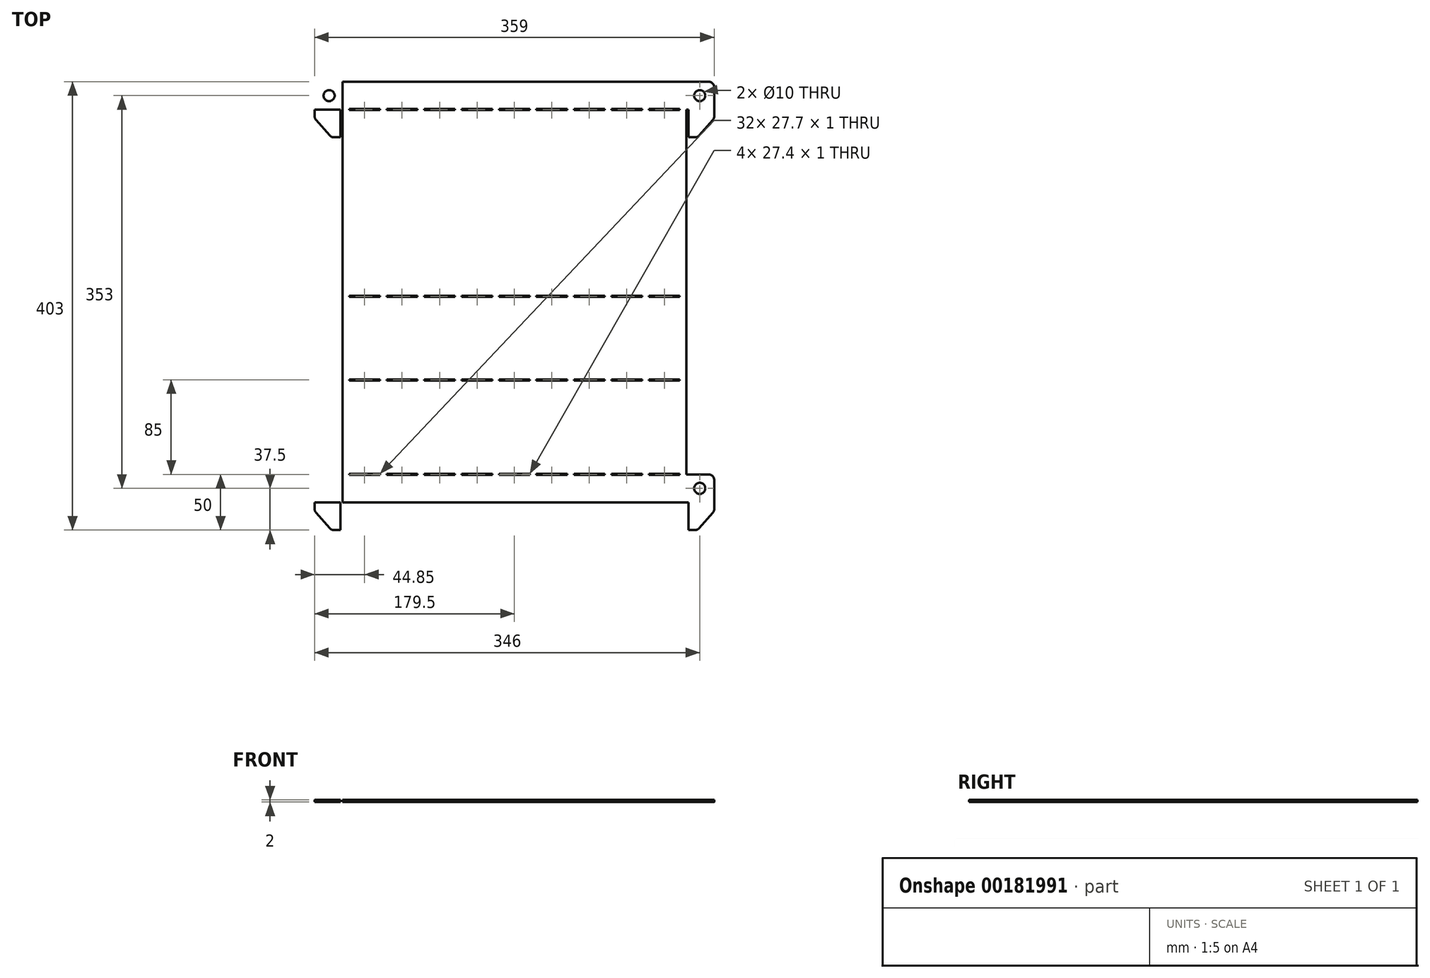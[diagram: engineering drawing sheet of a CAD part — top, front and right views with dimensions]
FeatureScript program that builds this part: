
annotation { "Feature Type Name" : "Feature", "Feature Type Description" : "" }
export const myFeature = defineFeature(function(context is Context, id is Id, definition is map)
    precondition{}
    {
        {
            var Q0;
            Q0=qCreatedBy(makeId("Top.planeOp"),FACE);
            var sketch = newSketch(context, id + "F0", { "sketchPlane" : qUnion([Q0])});
            skLineSegment(sketch, "E0.bottom", {"start": v(0, 0) * mm, "end": v(154.5, 0) * mm});
            skLineSegment(sketch, "E0.top", {"start": v(0, 378) * mm, "end": v(154.5, 378) * mm});
            skLineSegment(sketch, "E0.left", {"start": v(0, 0) * mm, "end": v(0, 352.5) * mm});
            skLineSegment(sketch, "E0.right", {"start": v(154.5, 0) * mm, "end": v(154.5, 378) * mm});
            skCircle(sketch, "E1", {"center": v(166.5, 365.5) * mm, "radius": 5 * mm});
            skLineSegment(sketch, "E2", {"start": v(154.5, 378) * mm, "end": v(174.5, 378) * mm});
            skLineSegment(sketch, "E3", {"start": v(154.5, 353) * mm, "end": v(0, 353) * mm});
            skLineSegment(sketch, "E4", {"start": v(0, 185) * mm, "end": v(148.5, 185) * mm});
            skLineSegment(sketch, "E5", {"start": v(0, 110) * mm, "end": v(154.5, 110) * mm});
            skLineSegment(sketch, "E6", {"start": v(0, 25) * mm, "end": v(154.5, 25) * mm});
            skPoint(sketch, "E7.visualSharp", {"position": v(179.5, 353) * mm});
            skLineSegment(sketch, "E8.bottom", {"start": v(148.5, 353) * mm, "end": v(120.8, 353) * mm});
            skLineSegment(sketch, "E8.top", {"start": v(148.5, 352.5) * mm, "end": v(120.8, 352.5) * mm});
            skLineSegment(sketch, "E8.left", {"start": v(148.5, 353) * mm, "end": v(148.5, 352.5) * mm});
            skLineSegment(sketch, "E8.right", {"start": v(120.8, 353) * mm, "end": v(120.8, 352.5) * mm});
            skLineSegment(sketch, "E9.bottom", {"start": v(114.8, 353) * mm, "end": v(87.1, 353) * mm});
            skLineSegment(sketch, "E9.top", {"start": v(114.8, 352.5) * mm, "end": v(87.1, 352.5) * mm});
            skLineSegment(sketch, "E9.left", {"start": v(114.8, 353) * mm, "end": v(114.8, 352.5) * mm});
            skLineSegment(sketch, "E9.right", {"start": v(87.1, 353) * mm, "end": v(87.1, 352.5) * mm});
            skLineSegment(sketch, "E10.bottom", {"start": v(81.1, 353) * mm, "end": v(53.4, 353) * mm});
            skLineSegment(sketch, "E10.top", {"start": v(81.1, 352.5) * mm, "end": v(53.4, 352.5) * mm});
            skLineSegment(sketch, "E10.left", {"start": v(81.1, 353) * mm, "end": v(81.1, 352.5) * mm});
            skLineSegment(sketch, "E10.right", {"start": v(53.4, 353) * mm, "end": v(53.4, 352.5) * mm});
            skLineSegment(sketch, "E11.bottom", {"start": v(47.4, 353) * mm, "end": v(19.7, 353) * mm});
            skLineSegment(sketch, "E11.top", {"start": v(47.4, 352.5) * mm, "end": v(19.7, 352.5) * mm});
            skLineSegment(sketch, "E11.left", {"start": v(47.4, 353) * mm, "end": v(47.4, 352.5) * mm});
            skLineSegment(sketch, "E11.right", {"start": v(19.7, 353) * mm, "end": v(19.7, 352.5) * mm});
            skLineSegment(sketch, "E12.bottom", {"start": v(13.7, 353) * mm, "end": v(0, 353) * mm});
            skLineSegment(sketch, "E12.top", {"start": v(13.7, 352.5) * mm, "end": v(0, 352.5) * mm});
            skLineSegment(sketch, "E12.left", {"start": v(13.7, 353) * mm, "end": v(13.7, 352.5) * mm});
            skLineSegment(sketch, "E12.right", {"start": v(0, 353) * mm, "end": v(0, 352.5) * mm});
            skLineSegment(sketch, "E13.MirrorCS", {"start": v(120.8, 353) * mm, "end": v(120.8, 353.5) * mm});
            skLineSegment(sketch, "E14.MirrorCS", {"start": v(148.5, 353.5) * mm, "end": v(120.8, 353.5) * mm});
            skLineSegment(sketch, "E15.MirrorCS", {"start": v(148.5, 353) * mm, "end": v(148.5, 353.5) * mm});
            skLineSegment(sketch, "E16.MirrorCS", {"start": v(114.8, 353) * mm, "end": v(114.8, 353.5) * mm});
            skLineSegment(sketch, "E17.MirrorCS", {"start": v(114.8, 353.5) * mm, "end": v(87.1, 353.5) * mm});
            skLineSegment(sketch, "E18.MirrorCS", {"start": v(87.1, 353) * mm, "end": v(87.1, 353.5) * mm});
            skLineSegment(sketch, "E19.MirrorCS", {"start": v(81.1, 353) * mm, "end": v(81.1, 353.5) * mm});
            skLineSegment(sketch, "E20.MirrorCS", {"start": v(81.1, 353.5) * mm, "end": v(53.4, 353.5) * mm});
            skLineSegment(sketch, "E21.MirrorCS", {"start": v(53.4, 353) * mm, "end": v(53.4, 353.5) * mm});
            skLineSegment(sketch, "E22.MirrorCS", {"start": v(47.4, 353) * mm, "end": v(47.4, 353.5) * mm});
            skLineSegment(sketch, "E23.MirrorCS", {"start": v(47.4, 353.5) * mm, "end": v(19.7, 353.5) * mm});
            skLineSegment(sketch, "E24.MirrorCS", {"start": v(19.7, 353) * mm, "end": v(19.7, 353.5) * mm});
            skLineSegment(sketch, "E25.MirrorCS", {"start": v(13.7, 353) * mm, "end": v(13.7, 353.5) * mm});
            skLineSegment(sketch, "E26.MirrorCS", {"start": v(13.7, 353.5) * mm, "end": v(0, 353.5) * mm});
            skLineSegment(sketch, "E27.MirrorCS", {"start": v(0, 353) * mm, "end": v(0, 353.5) * mm});
            skLineSegment(sketch, "E28", {"start": v(111.78, 185) * mm, "end": v(0, 185) * mm});
            skLineSegment(sketch, "E29.bottom", {"start": v(148.5, 185) * mm, "end": v(120.8, 185) * mm});
            skLineSegment(sketch, "E29.top", {"start": v(148.5, 184.5) * mm, "end": v(120.8, 184.5) * mm});
            skLineSegment(sketch, "E29.left", {"start": v(148.5, 185) * mm, "end": v(148.5, 184.5) * mm});
            skLineSegment(sketch, "E29.right", {"start": v(120.8, 185) * mm, "end": v(120.8, 184.5) * mm});
            skLineSegment(sketch, "E30.bottom", {"start": v(114.8, 185) * mm, "end": v(87.1, 185) * mm});
            skLineSegment(sketch, "E30.top", {"start": v(114.8, 184.5) * mm, "end": v(87.1, 184.5) * mm});
            skLineSegment(sketch, "E30.left", {"start": v(114.8, 185) * mm, "end": v(114.8, 184.5) * mm});
            skLineSegment(sketch, "E30.right", {"start": v(87.1, 185) * mm, "end": v(87.1, 184.5) * mm});
            skLineSegment(sketch, "E31.bottom", {"start": v(81.1, 185) * mm, "end": v(53.4, 185) * mm});
            skLineSegment(sketch, "E31.top", {"start": v(81.1, 184.5) * mm, "end": v(53.4, 184.5) * mm});
            skLineSegment(sketch, "E31.left", {"start": v(81.1, 185) * mm, "end": v(81.1, 184.5) * mm});
            skLineSegment(sketch, "E31.right", {"start": v(53.4, 185) * mm, "end": v(53.4, 184.5) * mm});
            skLineSegment(sketch, "E32.bottom", {"start": v(47.4, 185) * mm, "end": v(19.7, 185) * mm});
            skLineSegment(sketch, "E32.top", {"start": v(47.4, 184.5) * mm, "end": v(19.7, 184.5) * mm});
            skLineSegment(sketch, "E32.left", {"start": v(47.4, 185) * mm, "end": v(47.4, 184.5) * mm});
            skLineSegment(sketch, "E32.right", {"start": v(19.7, 185) * mm, "end": v(19.7, 184.5) * mm});
            skLineSegment(sketch, "E33.bottom", {"start": v(13.7, 185) * mm, "end": v(0, 185) * mm});
            skLineSegment(sketch, "E33.top", {"start": v(13.7, 184.5) * mm, "end": v(0, 184.5) * mm});
            skLineSegment(sketch, "E33.left", {"start": v(13.7, 185) * mm, "end": v(13.7, 184.5) * mm});
            skLineSegment(sketch, "E34.MirrorCS", {"start": v(120.8, 185) * mm, "end": v(120.8, 185.5) * mm});
            skLineSegment(sketch, "E35.MirrorCS", {"start": v(148.5, 185.5) * mm, "end": v(120.8, 185.5) * mm});
            skLineSegment(sketch, "E36.MirrorCS", {"start": v(148.5, 185) * mm, "end": v(148.5, 185.5) * mm});
            skLineSegment(sketch, "E37.MirrorCS", {"start": v(114.8, 185) * mm, "end": v(114.8, 185.5) * mm});
            skLineSegment(sketch, "E38.MirrorCS", {"start": v(114.8, 185.5) * mm, "end": v(87.1, 185.5) * mm});
            skLineSegment(sketch, "E39.MirrorCS", {"start": v(87.1, 185) * mm, "end": v(87.1, 185.5) * mm});
            skLineSegment(sketch, "E40.MirrorCS", {"start": v(81.1, 185) * mm, "end": v(81.1, 185.5) * mm});
            skLineSegment(sketch, "E41.MirrorCS", {"start": v(81.1, 185.5) * mm, "end": v(53.4, 185.5) * mm});
            skLineSegment(sketch, "E42.MirrorCS", {"start": v(53.4, 185) * mm, "end": v(53.4, 185.5) * mm});
            skLineSegment(sketch, "E43.MirrorCS", {"start": v(47.4, 185) * mm, "end": v(47.4, 185.5) * mm});
            skLineSegment(sketch, "E44.MirrorCS", {"start": v(47.4, 185.5) * mm, "end": v(19.7, 185.5) * mm});
            skLineSegment(sketch, "E45.MirrorCS", {"start": v(19.7, 185) * mm, "end": v(19.7, 185.5) * mm});
            skLineSegment(sketch, "E46.MirrorCS", {"start": v(13.7, 185) * mm, "end": v(13.7, 185.5) * mm});
            skLineSegment(sketch, "E47.MirrorCS", {"start": v(13.7, 185.5) * mm, "end": v(0, 185.5) * mm});
            skLineSegment(sketch, "E48", {"start": v(148.5, 110) * mm, "end": v(0, 110) * mm});
            skLineSegment(sketch, "E49.bottom", {"start": v(148.5, 110) * mm, "end": v(120.8, 110) * mm});
            skLineSegment(sketch, "E49.top", {"start": v(148.5, 109.5) * mm, "end": v(120.8, 109.5) * mm});
            skLineSegment(sketch, "E49.left", {"start": v(148.5, 110) * mm, "end": v(148.5, 109.5) * mm});
            skLineSegment(sketch, "E49.right", {"start": v(120.8, 110) * mm, "end": v(120.8, 109.5) * mm});
            skLineSegment(sketch, "E50.bottom", {"start": v(114.8, 110) * mm, "end": v(87.1, 110) * mm});
            skLineSegment(sketch, "E50.top", {"start": v(114.8, 109.5) * mm, "end": v(87.1, 109.5) * mm});
            skLineSegment(sketch, "E50.left", {"start": v(114.8, 110) * mm, "end": v(114.8, 109.5) * mm});
            skLineSegment(sketch, "E50.right", {"start": v(87.1, 110) * mm, "end": v(87.1, 109.5) * mm});
            skLineSegment(sketch, "E51.bottom", {"start": v(81.1, 110) * mm, "end": v(53.4, 110) * mm});
            skLineSegment(sketch, "E51.top", {"start": v(81.1, 109.5) * mm, "end": v(53.4, 109.5) * mm});
            skLineSegment(sketch, "E51.left", {"start": v(81.1, 110) * mm, "end": v(81.1, 109.5) * mm});
            skLineSegment(sketch, "E51.right", {"start": v(53.4, 110) * mm, "end": v(53.4, 109.5) * mm});
            skLineSegment(sketch, "E52.bottom", {"start": v(47.4, 110) * mm, "end": v(19.7, 110) * mm});
            skLineSegment(sketch, "E52.top", {"start": v(47.4, 109.5) * mm, "end": v(19.7, 109.5) * mm});
            skLineSegment(sketch, "E52.left", {"start": v(47.4, 110) * mm, "end": v(47.4, 109.5) * mm});
            skLineSegment(sketch, "E52.right", {"start": v(19.7, 110) * mm, "end": v(19.7, 109.5) * mm});
            skLineSegment(sketch, "E53.bottom", {"start": v(13.7, 110) * mm, "end": v(0, 110) * mm});
            skLineSegment(sketch, "E53.top", {"start": v(13.7, 109.5) * mm, "end": v(0, 109.5) * mm});
            skLineSegment(sketch, "E53.left", {"start": v(13.7, 110) * mm, "end": v(13.7, 109.5) * mm});
            skLineSegment(sketch, "E54.MirrorCS", {"start": v(120.8, 110) * mm, "end": v(120.8, 110.5) * mm});
            skLineSegment(sketch, "E55.MirrorCS", {"start": v(148.5, 110.5) * mm, "end": v(120.8, 110.5) * mm});
            skLineSegment(sketch, "E56.MirrorCS", {"start": v(148.5, 110) * mm, "end": v(148.5, 110.5) * mm});
            skLineSegment(sketch, "E57.MirrorCS", {"start": v(114.8, 110) * mm, "end": v(114.8, 110.5) * mm});
            skLineSegment(sketch, "E58.MirrorCS", {"start": v(114.8, 110.5) * mm, "end": v(87.1, 110.5) * mm});
            skLineSegment(sketch, "E59.MirrorCS", {"start": v(87.1, 110) * mm, "end": v(87.1, 110.5) * mm});
            skLineSegment(sketch, "E60.MirrorCS", {"start": v(81.1, 110) * mm, "end": v(81.1, 110.5) * mm});
            skLineSegment(sketch, "E61.MirrorCS", {"start": v(81.1, 110.5) * mm, "end": v(53.4, 110.5) * mm});
            skLineSegment(sketch, "E62.MirrorCS", {"start": v(53.4, 110) * mm, "end": v(53.4, 110.5) * mm});
            skLineSegment(sketch, "E63.MirrorCS", {"start": v(47.4, 110) * mm, "end": v(47.4, 110.5) * mm});
            skLineSegment(sketch, "E64.MirrorCS", {"start": v(47.4, 110.5) * mm, "end": v(19.7, 110.5) * mm});
            skLineSegment(sketch, "E65.MirrorCS", {"start": v(19.7, 110) * mm, "end": v(19.7, 110.5) * mm});
            skLineSegment(sketch, "E66.MirrorCS", {"start": v(13.7, 110) * mm, "end": v(13.7, 110.5) * mm});
            skLineSegment(sketch, "E67.MirrorCS", {"start": v(13.7, 110.5) * mm, "end": v(0, 110.5) * mm});
            skLineSegment(sketch, "E68", {"start": v(148.5, 25) * mm, "end": v(0, 25) * mm});
            skLineSegment(sketch, "E69.bottom", {"start": v(148.5, 25) * mm, "end": v(120.8, 25) * mm});
            skLineSegment(sketch, "E69.top", {"start": v(148.5, 24.5) * mm, "end": v(120.8, 24.5) * mm});
            skLineSegment(sketch, "E69.left", {"start": v(148.5, 25) * mm, "end": v(148.5, 24.5) * mm});
            skLineSegment(sketch, "E69.right", {"start": v(120.8, 25) * mm, "end": v(120.8, 24.5) * mm});
            skLineSegment(sketch, "E70.bottom", {"start": v(114.8, 25) * mm, "end": v(87.1, 25) * mm});
            skLineSegment(sketch, "E70.top", {"start": v(114.8, 24.5) * mm, "end": v(87.1, 24.5) * mm});
            skLineSegment(sketch, "E70.left", {"start": v(114.8, 25) * mm, "end": v(114.8, 24.5) * mm});
            skLineSegment(sketch, "E70.right", {"start": v(87.1, 25) * mm, "end": v(87.1, 24.5) * mm});
            skLineSegment(sketch, "E71.bottom", {"start": v(81.1, 25) * mm, "end": v(53.4, 25) * mm});
            skLineSegment(sketch, "E71.top", {"start": v(81.1, 24.5) * mm, "end": v(53.4, 24.5) * mm});
            skLineSegment(sketch, "E71.left", {"start": v(81.1, 25) * mm, "end": v(81.1, 24.5) * mm});
            skLineSegment(sketch, "E71.right", {"start": v(53.4, 25) * mm, "end": v(53.4, 24.5) * mm});
            skLineSegment(sketch, "E72.bottom", {"start": v(47.4, 25) * mm, "end": v(19.7, 25) * mm});
            skLineSegment(sketch, "E72.top", {"start": v(47.4, 24.5) * mm, "end": v(19.7, 24.5) * mm});
            skLineSegment(sketch, "E72.left", {"start": v(47.4, 25) * mm, "end": v(47.4, 24.5) * mm});
            skLineSegment(sketch, "E72.right", {"start": v(19.7, 25) * mm, "end": v(19.7, 24.5) * mm});
            skLineSegment(sketch, "E73.bottom", {"start": v(13.7, 25) * mm, "end": v(0, 25) * mm});
            skLineSegment(sketch, "E73.top", {"start": v(13.7, 24.5) * mm, "end": v(0, 24.5) * mm});
            skLineSegment(sketch, "E73.left", {"start": v(13.7, 25) * mm, "end": v(13.7, 24.5) * mm});
            skLineSegment(sketch, "E74.MirrorCS", {"start": v(120.8, 25) * mm, "end": v(120.8, 25.5) * mm});
            skLineSegment(sketch, "E75.MirrorCS", {"start": v(148.5, 25.5) * mm, "end": v(120.8, 25.5) * mm});
            skLineSegment(sketch, "E76.MirrorCS", {"start": v(148.5, 25) * mm, "end": v(148.5, 25.5) * mm});
            skLineSegment(sketch, "E77.MirrorCS", {"start": v(114.8, 25) * mm, "end": v(114.8, 25.5) * mm});
            skLineSegment(sketch, "E78.MirrorCS", {"start": v(114.8, 25.5) * mm, "end": v(87.1, 25.5) * mm});
            skLineSegment(sketch, "E79.MirrorCS", {"start": v(87.1, 25) * mm, "end": v(87.1, 25.5) * mm});
            skLineSegment(sketch, "E80.MirrorCS", {"start": v(81.1, 25) * mm, "end": v(81.1, 25.5) * mm});
            skLineSegment(sketch, "E81.MirrorCS", {"start": v(81.1, 25.5) * mm, "end": v(53.4, 25.5) * mm});
            skLineSegment(sketch, "E82.MirrorCS", {"start": v(53.4, 25) * mm, "end": v(53.4, 25.5) * mm});
            skLineSegment(sketch, "E83.MirrorCS", {"start": v(47.4, 25) * mm, "end": v(47.4, 25.5) * mm});
            skLineSegment(sketch, "E84.MirrorCS", {"start": v(47.4, 25.5) * mm, "end": v(19.7, 25.5) * mm});
            skLineSegment(sketch, "E85.MirrorCS", {"start": v(19.7, 25) * mm, "end": v(19.7, 25.5) * mm});
            skLineSegment(sketch, "E86.MirrorCS", {"start": v(13.7, 25) * mm, "end": v(13.7, 25.5) * mm});
            skLineSegment(sketch, "E87.MirrorCS", {"start": v(13.7, 25.5) * mm, "end": v(0, 25.5) * mm});
            skLineSegment(sketch, "E88", {"start": v(154.5, 25) * mm, "end": v(174.5, 25) * mm});
            skLineSegment(sketch, "E89", {"start": v(179.5, 20) * mm, "end": v(179.5, 0) * mm});
            skLineSegment(sketch, "E90", {"start": v(179.5, 0) * mm, "end": v(154.5, 0) * mm});
            skLineSegment(sketch, "E91", {"start": v(156.5, 0) * mm, "end": v(156.5, -25) * mm});
            skLineSegment(sketch, "E92", {"start": v(156.5, -25) * mm, "end": v(162.24, -25) * mm});
            skLineSegment(sketch, "E93", {"start": v(179.5, 0) * mm, "end": v(179.5, -6.1) * mm});
            skLineSegment(sketch, "E94", {"start": v(178.25, -9.42) * mm, "end": v(166, -23.3) * mm});
            skCircle(sketch, "E95", {"center": v(166.5, 12.5) * mm, "radius": 5 * mm});
            skPoint(sketch, "E96.visualSharp", {"position": v(179.5, 25) * mm});
            skArc(sketch, "E96.filletArc", {"start": v(179.5, 20) * mm, "mid": v(178.04, 23.54) * mm, "end": v(174.5, 25) * mm});
            skPoint(sketch, "E97.visualSharp", {"position": v(179.5, -8) * mm});
            skArc(sketch, "E97.filletArc", {"start": v(178.25, -9.42) * mm, "mid": v(179.18, -7.88) * mm, "end": v(179.5, -6.1) * mm});
            skPoint(sketch, "E98.visualSharp", {"position": v(164.5, -25) * mm});
            skArc(sketch, "E98.filletArc", {"start": v(162.24, -25) * mm, "mid": v(164.3, -24.56) * mm, "end": v(166, -23.3) * mm});
            skLineSegment(sketch, "E99.MirrorCS", {"start": v(-148.5, 25) * mm, "end": v(-148.5, 24.5) * mm});
            skLineSegment(sketch, "E100.MirrorCS", {"start": v(-13.7, 353.5) * mm, "end": v(0, 353.5) * mm});
            skLineSegment(sketch, "E101.MirrorCS", {"start": v(-13.7, 353) * mm, "end": v(-13.7, 352.5) * mm});
            skLineSegment(sketch, "E102.MirrorCS", {"start": v(-148.5, 185) * mm, "end": v(-148.5, 184.5) * mm});
            skLineSegment(sketch, "E103.MirrorCS", {"start": v(-114.8, 185) * mm, "end": v(-114.8, 184.5) * mm});
            skLineSegment(sketch, "E104.MirrorCS", {"start": v(-81.1, 353) * mm, "end": v(-81.1, 353.5) * mm});
            skLineSegment(sketch, "E105.MirrorCS", {"start": v(-13.7, 352.5) * mm, "end": v(0, 352.5) * mm});
            skLineSegment(sketch, "E106.MirrorCS", {"start": v(-81.1, 25) * mm, "end": v(-81.1, 25.5) * mm});
            skLineSegment(sketch, "E107.MirrorCS", {"start": v(-53.4, 110) * mm, "end": v(-53.4, 110.5) * mm});
            skLineSegment(sketch, "E108.MirrorCS", {"start": v(-114.8, 110) * mm, "end": v(-114.8, 110.5) * mm});
            skLineSegment(sketch, "E109.MirrorCS", {"start": v(-148.5, 353) * mm, "end": v(-148.5, 352.5) * mm});
            skLineSegment(sketch, "E110.MirrorCS", {"start": v(-47.4, 185) * mm, "end": v(-47.4, 184.5) * mm});
            skLineSegment(sketch, "E111.MirrorCS", {"start": v(-47.4, 110) * mm, "end": v(-47.4, 110.5) * mm});
            skLineSegment(sketch, "E112.MirrorCS", {"start": v(-47.4, 353) * mm, "end": v(-47.4, 353.5) * mm});
            skLineSegment(sketch, "E113.MirrorCS", {"start": v(-148.5, 25) * mm, "end": v(-148.5, 25.5) * mm});
            skLineSegment(sketch, "E114.MirrorCS", {"start": v(-120.8, 353) * mm, "end": v(-120.8, 352.5) * mm});
            skLineSegment(sketch, "E115.MirrorCS", {"start": v(-53.4, 25) * mm, "end": v(-53.4, 25.5) * mm});
            skLineSegment(sketch, "E116.MirrorCS", {"start": v(-47.4, 25) * mm, "end": v(-47.4, 25.5) * mm});
            skLineSegment(sketch, "E117.MirrorCS", {"start": v(-19.7, 110) * mm, "end": v(-19.7, 110.5) * mm});
            skLineSegment(sketch, "E118.MirrorCS", {"start": v(-13.7, 110) * mm, "end": v(-13.7, 110.5) * mm});
            skLineSegment(sketch, "E119.MirrorCS", {"start": v(-114.8, 353) * mm, "end": v(-114.8, 352.5) * mm});
            skLineSegment(sketch, "E120.MirrorCS", {"start": v(-114.8, 25) * mm, "end": v(-114.8, 25.5) * mm});
            skLineSegment(sketch, "E121.MirrorCS", {"start": v(-19.7, 25) * mm, "end": v(-19.7, 25.5) * mm});
            skLineSegment(sketch, "E122.MirrorCS", {"start": v(-120.8, 185) * mm, "end": v(-120.8, 184.5) * mm});
            skLineSegment(sketch, "E123.MirrorCS", {"start": v(-87.1, 353) * mm, "end": v(-87.1, 352.5) * mm});
            skLineSegment(sketch, "E124.MirrorCS", {"start": v(-13.7, 25) * mm, "end": v(-13.7, 25.5) * mm});
            skLineSegment(sketch, "E125.MirrorCS", {"start": v(-148.5, 110) * mm, "end": v(-148.5, 109.5) * mm});
            skLineSegment(sketch, "E126.MirrorCS", {"start": v(-120.8, 110) * mm, "end": v(-120.8, 110.5) * mm});
            skLineSegment(sketch, "E127.MirrorCS", {"start": v(-148.5, 185) * mm, "end": v(-148.5, 185.5) * mm});
            skLineSegment(sketch, "E128.MirrorCS", {"start": v(-19.7, 353) * mm, "end": v(-19.7, 353.5) * mm});
            skLineSegment(sketch, "E129.MirrorCS", {"start": v(-87.1, 185) * mm, "end": v(-87.1, 184.5) * mm});
            skLineSegment(sketch, "E130.MirrorCS", {"start": v(-87.1, 25) * mm, "end": v(-87.1, 24.5) * mm});
            skLineSegment(sketch, "E131.MirrorCS", {"start": v(-81.1, 110) * mm, "end": v(-81.1, 110.5) * mm});
            skLineSegment(sketch, "E132.MirrorCS", {"start": v(-53.4, 353) * mm, "end": v(-53.4, 352.5) * mm});
            skLineSegment(sketch, "E133.MirrorCS", {"start": v(-120.8, 25) * mm, "end": v(-120.8, 25.5) * mm});
            skLineSegment(sketch, "E134.MirrorCS", {"start": v(-148.5, 110) * mm, "end": v(-148.5, 110.5) * mm});
            skLineSegment(sketch, "E135.MirrorCS", {"start": v(-13.7, 353) * mm, "end": v(-13.7, 353.5) * mm});
            skLineSegment(sketch, "E136.MirrorCS", {"start": v(-81.1, 353) * mm, "end": v(-81.1, 352.5) * mm});
            skLineSegment(sketch, "E137.MirrorCS", {"start": v(-114.8, 185) * mm, "end": v(-114.8, 185.5) * mm});
            skLineSegment(sketch, "E138.MirrorCS", {"start": v(-13.7, 25) * mm, "end": v(-13.7, 24.5) * mm});
            skLineSegment(sketch, "E139.MirrorCS", {"start": v(-87.1, 185) * mm, "end": v(-87.1, 185.5) * mm});
            skLineSegment(sketch, "E140.MirrorCS", {"start": v(-53.4, 353) * mm, "end": v(-53.4, 353.5) * mm});
            skLineSegment(sketch, "E141.MirrorCS", {"start": v(-53.4, 110) * mm, "end": v(-53.4, 109.5) * mm});
            skLineSegment(sketch, "E142.MirrorCS", {"start": v(-114.8, 110) * mm, "end": v(-114.8, 109.5) * mm});
            skLineSegment(sketch, "E143.MirrorCS", {"start": v(-19.7, 185) * mm, "end": v(-19.7, 185.5) * mm});
            skLineSegment(sketch, "E144.MirrorCS", {"start": v(-81.1, 25) * mm, "end": v(-81.1, 24.5) * mm});
            skLineSegment(sketch, "E145.MirrorCS", {"start": v(-81.1, 185) * mm, "end": v(-81.1, 185.5) * mm});
            skLineSegment(sketch, "E146.MirrorCS", {"start": v(-87.1, 110) * mm, "end": v(-87.1, 109.5) * mm});
            skLineSegment(sketch, "E147.MirrorCS", {"start": v(-13.7, 185) * mm, "end": v(-13.7, 185.5) * mm});
            skLineSegment(sketch, "E148.MirrorCS", {"start": v(-19.7, 185) * mm, "end": v(-19.7, 184.5) * mm});
            skLineSegment(sketch, "E149.MirrorCS", {"start": v(-53.4, 25) * mm, "end": v(-53.4, 24.5) * mm});
            skLineSegment(sketch, "E150.MirrorCS", {"start": v(-120.8, 353) * mm, "end": v(-120.8, 353.5) * mm});
            skLineSegment(sketch, "E151.MirrorCS", {"start": v(-47.4, 110) * mm, "end": v(-47.4, 109.5) * mm});
            skLineSegment(sketch, "E152.MirrorCS", {"start": v(-19.7, 110) * mm, "end": v(-19.7, 109.5) * mm});
            skLineSegment(sketch, "E153.MirrorCS", {"start": v(-148.5, 353) * mm, "end": v(-148.5, 353.5) * mm});
            skLineSegment(sketch, "E154.MirrorCS", {"start": v(-114.8, 25) * mm, "end": v(-114.8, 24.5) * mm});
            skLineSegment(sketch, "E155.MirrorCS", {"start": v(-87.1, 110) * mm, "end": v(-87.1, 110.5) * mm});
            skLineSegment(sketch, "E156.MirrorCS", {"start": v(-13.7, 185) * mm, "end": v(-13.7, 184.5) * mm});
            skLineSegment(sketch, "E157.MirrorCS", {"start": v(-47.4, 25) * mm, "end": v(-47.4, 24.5) * mm});
            skLineSegment(sketch, "E158.MirrorCS", {"start": v(-114.8, 353) * mm, "end": v(-114.8, 353.5) * mm});
            skLineSegment(sketch, "E159.MirrorCS", {"start": v(-120.8, 185) * mm, "end": v(-120.8, 185.5) * mm});
            skLineSegment(sketch, "E160.MirrorCS", {"start": v(-19.7, 25) * mm, "end": v(-19.7, 24.5) * mm});
            skLineSegment(sketch, "E161.MirrorCS", {"start": v(-13.7, 110) * mm, "end": v(-13.7, 109.5) * mm});
            skLineSegment(sketch, "E162.MirrorCS", {"start": v(-81.1, 185) * mm, "end": v(-81.1, 184.5) * mm});
            skLineSegment(sketch, "E163.MirrorCS", {"start": v(-47.4, 353) * mm, "end": v(-47.4, 352.5) * mm});
            skLineSegment(sketch, "E164.MirrorCS", {"start": v(-13.7, 25.5) * mm, "end": v(0, 25.5) * mm});
            skLineSegment(sketch, "E165.MirrorCS", {"start": v(-87.1, 353) * mm, "end": v(-87.1, 353.5) * mm});
            skLineSegment(sketch, "E166.MirrorCS", {"start": v(-120.8, 110) * mm, "end": v(-120.8, 109.5) * mm});
            skLineSegment(sketch, "E167.MirrorCS", {"start": v(-53.4, 185) * mm, "end": v(-53.4, 185.5) * mm});
            skLineSegment(sketch, "E168.MirrorCS", {"start": v(-53.4, 185) * mm, "end": v(-53.4, 184.5) * mm});
            skLineSegment(sketch, "E169.MirrorCS", {"start": v(-19.7, 353) * mm, "end": v(-19.7, 352.5) * mm});
            skLineSegment(sketch, "E170.MirrorCS", {"start": v(-120.8, 25) * mm, "end": v(-120.8, 24.5) * mm});
            skLineSegment(sketch, "E171.MirrorCS", {"start": v(-47.4, 185) * mm, "end": v(-47.4, 185.5) * mm});
            skLineSegment(sketch, "E172.MirrorCS", {"start": v(-13.7, 353) * mm, "end": v(0, 353) * mm});
            skLineSegment(sketch, "E173.MirrorCS", {"start": v(-87.1, 25) * mm, "end": v(-87.1, 25.5) * mm});
            skLineSegment(sketch, "E174.MirrorCS", {"start": v(-81.1, 110) * mm, "end": v(-81.1, 109.5) * mm});
            skLineSegment(sketch, "E175.MirrorCS", {"start": v(-13.7, 185) * mm, "end": v(0, 185) * mm});
            skLineSegment(sketch, "E176.MirrorCS", {"start": v(-13.7, 110.5) * mm, "end": v(0, 110.5) * mm});
            skLineSegment(sketch, "E177.MirrorCS", {"start": v(-13.7, 25) * mm, "end": v(0, 25) * mm});
            skLineSegment(sketch, "E178.MirrorCS", {"start": v(-13.7, 185.5) * mm, "end": v(0, 185.5) * mm});
            skLineSegment(sketch, "E179.MirrorCS", {"start": v(-13.7, 184.5) * mm, "end": v(0, 184.5) * mm});
            skLineSegment(sketch, "E180.MirrorCS", {"start": v(-13.7, 110) * mm, "end": v(0, 110) * mm});
            skLineSegment(sketch, "E181.MirrorCS", {"start": v(-13.7, 109.5) * mm, "end": v(0, 109.5) * mm});
            skLineSegment(sketch, "E182.MirrorCS", {"start": v(-13.7, 24.5) * mm, "end": v(0, 24.5) * mm});
            skLineSegment(sketch, "E183.MirrorCS", {"start": v(-47.4, 110) * mm, "end": v(-19.7, 110) * mm});
            skLineSegment(sketch, "E184.MirrorCS", {"start": v(-156.5, -25) * mm, "end": v(-162.24, -25) * mm});
            skArc(sketch, "E185.MirrorCS", {"start": v(-162.24, -25) * mm, "mid": v(-164.3, -24.56) * mm, "end": v(-166, -23.3) * mm});
            skLineSegment(sketch, "E186.MirrorCS", {"start": v(-47.4, 25) * mm, "end": v(-19.7, 25) * mm});
            skLineSegment(sketch, "E187.MirrorCS", {"start": v(-47.4, 185.5) * mm, "end": v(-19.7, 185.5) * mm});
            skLineSegment(sketch, "E188.MirrorCS", {"start": v(-81.1, 24.5) * mm, "end": v(-53.4, 24.5) * mm});
            skArc(sketch, "E189.MirrorCS", {"start": v(-178.25, -9.42) * mm, "mid": v(-179.18, -7.88) * mm, "end": v(-179.5, -6.1) * mm});
            skLineSegment(sketch, "E190.MirrorCS", {"start": v(-47.4, 110.5) * mm, "end": v(-19.7, 110.5) * mm});
            skLineSegment(sketch, "E191.MirrorCS", {"start": v(-114.8, 353) * mm, "end": v(-87.1, 353) * mm});
            skLineSegment(sketch, "E192.MirrorCS", {"start": v(-148.5, 185) * mm, "end": v(-120.8, 185) * mm});
            skLineSegment(sketch, "E193.MirrorCS", {"start": v(-47.4, 25.5) * mm, "end": v(-19.7, 25.5) * mm});
            skLineSegment(sketch, "E194.MirrorCS", {"start": v(-148.5, 110) * mm, "end": v(-120.8, 110) * mm});
            skLineSegment(sketch, "E195.MirrorCS", {"start": v(-179.5, 0) * mm, "end": v(-179.5, -6.1) * mm});
            skLineSegment(sketch, "E196.MirrorCS", {"start": v(-114.8, 185) * mm, "end": v(-87.1, 185) * mm});
            skLineSegment(sketch, "E197.MirrorCS", {"start": v(-81.1, 353) * mm, "end": v(-53.4, 353) * mm});
            skLineSegment(sketch, "E198.MirrorCS", {"start": v(-148.5, 25) * mm, "end": v(-120.8, 25) * mm});
            skLineSegment(sketch, "E199.MirrorCS", {"start": v(-178.25, -9.42) * mm, "end": v(-166, -23.3) * mm});
            skLineSegment(sketch, "E200.MirrorCS", {"start": v(-114.8, 109.5) * mm, "end": v(-87.1, 109.5) * mm});
            skLineSegment(sketch, "E201.MirrorCS", {"start": v(-114.8, 110) * mm, "end": v(-87.1, 110) * mm});
            skLineSegment(sketch, "E202.MirrorCS", {"start": v(-148.5, 352.5) * mm, "end": v(-120.8, 352.5) * mm});
            skLineSegment(sketch, "E203.MirrorCS", {"start": v(-81.1, 185) * mm, "end": v(-53.4, 185) * mm});
            skLineSegment(sketch, "E204.MirrorCS", {"start": v(-47.4, 353) * mm, "end": v(-19.7, 353) * mm});
            skLineSegment(sketch, "E205.MirrorCS", {"start": v(-47.4, 184.5) * mm, "end": v(-19.7, 184.5) * mm});
            skArc(sketch, "E206.MirrorCS", {"start": v(-179.5, 20) * mm, "mid": v(-178.04, 23.54) * mm, "end": v(-174.5, 25) * mm});
            skLineSegment(sketch, "E207.MirrorCS", {"start": v(-114.8, 25) * mm, "end": v(-87.1, 25) * mm});
            skLineSegment(sketch, "E208.MirrorCS", {"start": v(-81.1, 25.5) * mm, "end": v(-53.4, 25.5) * mm});
            skLineSegment(sketch, "E209.MirrorCS", {"start": v(-47.4, 109.5) * mm, "end": v(-19.7, 109.5) * mm});
            skLineSegment(sketch, "E210.MirrorCS", {"start": v(-148.5, 184.5) * mm, "end": v(-120.8, 184.5) * mm});
            skLineSegment(sketch, "E211.MirrorCS", {"start": v(-114.8, 352.5) * mm, "end": v(-87.1, 352.5) * mm});
            skLineSegment(sketch, "E212.MirrorCS", {"start": v(-47.4, 24.5) * mm, "end": v(-19.7, 24.5) * mm});
            skLineSegment(sketch, "E213.MirrorCS", {"start": v(-81.1, 110) * mm, "end": v(-53.4, 110) * mm});
            skLineSegment(sketch, "E214.MirrorCS", {"start": v(-148.5, 109.5) * mm, "end": v(-120.8, 109.5) * mm});
            skLineSegment(sketch, "E215.MirrorCS", {"start": v(-114.8, 184.5) * mm, "end": v(-87.1, 184.5) * mm});
            skLineSegment(sketch, "E216.MirrorCS", {"start": v(-81.1, 352.5) * mm, "end": v(-53.4, 352.5) * mm});
            skLineSegment(sketch, "E217.MirrorCS", {"start": v(-148.5, 24.5) * mm, "end": v(-120.8, 24.5) * mm});
            skCircle(sketch, "E218.MirrorC", {"center": v(-166.5, 12.5) * mm, "radius": 5 * mm});
            skLineSegment(sketch, "E219.MirrorCS", {"start": v(-148.5, 110.5) * mm, "end": v(-120.8, 110.5) * mm});
            skLineSegment(sketch, "E220.MirrorCS", {"start": v(-148.5, 25.5) * mm, "end": v(-120.8, 25.5) * mm});
            skLineSegment(sketch, "E221.MirrorCS", {"start": v(-81.1, 184.5) * mm, "end": v(-53.4, 184.5) * mm});
            skLineSegment(sketch, "E222.MirrorCS", {"start": v(-47.4, 352.5) * mm, "end": v(-19.7, 352.5) * mm});
            skLineSegment(sketch, "E223.MirrorCS", {"start": v(-114.8, 24.5) * mm, "end": v(-87.1, 24.5) * mm});
            skLineSegment(sketch, "E224.MirrorCS", {"start": v(-114.8, 110.5) * mm, "end": v(-87.1, 110.5) * mm});
            skLineSegment(sketch, "E225.MirrorCS", {"start": v(-111.78, 185) * mm, "end": v(0, 185) * mm});
            skLineSegment(sketch, "E226.MirrorCS", {"start": v(-148.5, 353.5) * mm, "end": v(-120.8, 353.5) * mm});
            skLineSegment(sketch, "E227.MirrorCS", {"start": v(-148.5, 110) * mm, "end": v(0, 110) * mm});
            skCircle(sketch, "E228.MirrorC", {"center": v(-166.5, 365.5) * mm, "radius": 5 * mm});
            skLineSegment(sketch, "E229.MirrorCS", {"start": v(-148.5, 25) * mm, "end": v(0, 25) * mm});
            skLineSegment(sketch, "E230.MirrorCS", {"start": v(-114.8, 353.5) * mm, "end": v(-87.1, 353.5) * mm});
            skLineSegment(sketch, "E231.MirrorCS", {"start": v(-148.5, 185.5) * mm, "end": v(-120.8, 185.5) * mm});
            skLineSegment(sketch, "E232.MirrorCS", {"start": v(-114.8, 185.5) * mm, "end": v(-87.1, 185.5) * mm});
            skLineSegment(sketch, "E233.MirrorCS", {"start": v(-81.1, 353.5) * mm, "end": v(-53.4, 353.5) * mm});
            skLineSegment(sketch, "E234.MirrorCS", {"start": v(-81.1, 109.5) * mm, "end": v(-53.4, 109.5) * mm});
            skLineSegment(sketch, "E235.MirrorCS", {"start": v(-179.5, 20) * mm, "end": v(-179.5, 0) * mm});
            skLineSegment(sketch, "E236.MirrorCS", {"start": v(-156.5, 0) * mm, "end": v(-156.5, -25) * mm});
            skPoint(sketch, "E237.MirrorP", {"position": v(-164.5, -25) * mm});
            skLineSegment(sketch, "E238.MirrorCS", {"start": v(0, 110) * mm, "end": v(-154.5, 110) * mm});
            skLineSegment(sketch, "E239.MirrorCS", {"start": v(0, 25) * mm, "end": v(-154.5, 25) * mm});
            skLineSegment(sketch, "E240.MirrorCS", {"start": v(-154.5, 378) * mm, "end": v(-174.5, 378) * mm});
            skLineSegment(sketch, "E241.MirrorCS", {"start": v(-154.5, 353) * mm, "end": v(0, 353) * mm});
            skLineSegment(sketch, "E242.MirrorCS", {"start": v(0, 185) * mm, "end": v(-148.5, 185) * mm});
            skPoint(sketch, "E243.MirrorP", {"position": v(-179.5, 25) * mm});
            skLineSegment(sketch, "E244.MirrorCS", {"start": v(-81.1, 185.5) * mm, "end": v(-53.4, 185.5) * mm});
            skLineSegment(sketch, "E245.MirrorCS", {"start": v(-47.4, 353.5) * mm, "end": v(-19.7, 353.5) * mm});
            skLineSegment(sketch, "E246.MirrorCS", {"start": v(-154.5, 25) * mm, "end": v(-174.5, 25) * mm});
            skLineSegment(sketch, "E247.MirrorCS", {"start": v(-114.8, 25.5) * mm, "end": v(-87.1, 25.5) * mm});
            skLineSegment(sketch, "E248.MirrorCS", {"start": v(-179.5, 0) * mm, "end": v(-154.5, 0) * mm});
            skPoint(sketch, "E249.MirrorP", {"position": v(-179.5, -8) * mm});
            skLineSegment(sketch, "E250.MirrorCS", {"start": v(-148.5, 353) * mm, "end": v(-120.8, 353) * mm});
            skLineSegment(sketch, "E251.MirrorCS", {"start": v(-47.4, 185) * mm, "end": v(-19.7, 185) * mm});
            skLineSegment(sketch, "E252.MirrorCS", {"start": v(-81.1, 25) * mm, "end": v(-53.4, 25) * mm});
            skLineSegment(sketch, "E253.MirrorCS", {"start": v(-81.1, 110.5) * mm, "end": v(-53.4, 110.5) * mm});
            skLineSegment(sketch, "E254.MirrorCS", {"start": v(0, 0) * mm, "end": v(-154.5, 0) * mm});
            skLineSegment(sketch, "E255.MirrorCS", {"start": v(0, 378) * mm, "end": v(-154.5, 378) * mm});
            skLineSegment(sketch, "E256.MirrorCS", {"start": v(-154.5, 0) * mm, "end": v(-154.5, 378) * mm});
            skLineSegment(sketch, "E257.trimOffspring", {"start": v(0, 353.5) * mm, "end": v(0, 378) * mm});
            skPoint(sketch, "E258.MirrorCS.end.orphan", {"position": v(0, 353.5) * mm});
            skPoint(sketch, "E258.MirrorCS.start.orphan", {"position": v(0, 353) * mm});
            skLineSegment(sketch, "E259", {"start": v(-154.5, 353) * mm, "end": v(-179.5, 353) * mm});
            skLineSegment(sketch, "E260", {"start": v(-179.5, 353) * mm, "end": v(-179.5, 373) * mm});
            skLineSegment(sketch, "E261", {"start": v(-156.5, 353) * mm, "end": v(-156.5, 328) * mm});
            skLineSegment(sketch, "E262", {"start": v(-156.5, 328) * mm, "end": v(-162.24, 328) * mm});
            skLineSegment(sketch, "E263", {"start": v(-179.5, 353) * mm, "end": v(-179.5, 346.9) * mm});
            skLineSegment(sketch, "E264", {"start": v(-178.25, 343.58) * mm, "end": v(-166, 329.7) * mm});
            skPoint(sketch, "E265.visualSharp", {"position": v(-164.5, 328) * mm});
            skArc(sketch, "E265.filletArc", {"start": v(-166, 329.7) * mm, "mid": v(-164.3, 328.44) * mm, "end": v(-162.24, 328) * mm});
            skPoint(sketch, "E266.visualSharp", {"position": v(-179.5, 345) * mm});
            skArc(sketch, "E266.filletArc", {"start": v(-179.5, 346.9) * mm, "mid": v(-179.18, 345.12) * mm, "end": v(-178.25, 343.58) * mm});
            skPoint(sketch, "E267.visualSharp", {"position": v(-179.5, 378) * mm});
            skArc(sketch, "E267.filletArc", {"start": v(-174.5, 378) * mm, "mid": v(-178.04, 376.54) * mm, "end": v(-179.5, 373) * mm});
            skLineSegment(sketch, "E268", {"start": v(154.5, 353) * mm, "end": v(179.5, 353) * mm});
            skLineSegment(sketch, "E269", {"start": v(179.5, 373) * mm, "end": v(179.5, 353) * mm});
            skLineSegment(sketch, "E270", {"start": v(179.5, 353) * mm, "end": v(179.5, 346.9) * mm});
            skLineSegment(sketch, "E271", {"start": v(156.5, 353) * mm, "end": v(156.5, 328) * mm});
            skLineSegment(sketch, "E272", {"start": v(156.5, 328) * mm, "end": v(162.24, 328) * mm});
            skLineSegment(sketch, "E273", {"start": v(166, 329.7) * mm, "end": v(178.25, 343.58) * mm});
            skPoint(sketch, "E274.visualSharp", {"position": v(179.5, 345) * mm});
            skArc(sketch, "E274.filletArc", {"start": v(178.25, 343.58) * mm, "mid": v(179.18, 345.12) * mm, "end": v(179.5, 346.9) * mm});
            skPoint(sketch, "E275.visualSharp", {"position": v(164.5, 328) * mm});
            skArc(sketch, "E275.filletArc", {"start": v(162.24, 328) * mm, "mid": v(164.3, 328.44) * mm, "end": v(166, 329.7) * mm});
            skPoint(sketch, "E276.visualSharp", {"position": v(179.5, 378) * mm});
            skArc(sketch, "E276.filletArc", {"start": v(179.5, 373) * mm, "mid": v(178.04, 376.54) * mm, "end": v(174.5, 378) * mm});
            skSolve(sketch);
        }
        {
            var Q0;
            Q0=makeQuery(id+"F0.imprint","IMPRINT",FACE,{"disambiguationData":[TD([[makeQuery(id+"F0.imprint","IMPRINT",EDGE,{"derivedFrom":sQuery(id+"F0.wireOp",EDGE,"E228.MirrorC")}),1.0]])]});
            var Q1;
            {var subQ2=sQuery(id+"F0.wireOp",EDGE,"E261");Q1=makeQuery(id+"F0.imprint","IMPRINT",FACE,{"disambiguationData":[TD([[makeQuery(id+"F0.imprint","IMPRINT",EDGE,{"derivedFrom":subQ2}),-1.0]])]});}
            var Q2;
            {var subQ9=sQuery(id+"F0.wireOp",EDGE,"E104.MirrorCS");Q2=makeQuery(id+"F0.imprint","IMPRINT",FACE,{"disambiguationData":[TD([[makeQuery(id+"F0.imprint","IMPRINT",EDGE,{"derivedFrom":subQ9}),1.0]])]});}
            var Q3;
            {var subQ54=sQuery(id+"F0.wireOp",EDGE,"E102.MirrorCS");Q3=makeQuery(id+"F0.imprint","IMPRINT",FACE,{"disambiguationData":[TD([[makeQuery(id+"F0.imprint","IMPRINT",EDGE,{"derivedFrom":subQ54}),-1.0]])]});}
            var Q4;
            {var subQ12=sQuery(id+"F0.wireOp",EDGE,"E0.top");Q4=makeQuery(id+"F0.imprint","IMPRINT",FACE,{"disambiguationData":[TD([[makeQuery(id+"F0.imprint","IMPRINT",EDGE,{"derivedFrom":subQ12}),-1.0]])]});}
            var Q5;
            {var subQ37=sQuery(id+"F0.wireOp",EDGE,"E5");Q5=makeQuery(id+"F0.imprint","IMPRINT",FACE,{"disambiguationData":[TD([[makeQuery(id+"F0.imprint","IMPRINT",EDGE,{"derivedFrom":subQ37}),1.0]])]});}
            var Q6;
            Q6=makeQuery(id+"F0.imprint","IMPRINT",FACE,{"disambiguationData":[TD([[makeQuery(id+"F0.imprint","IMPRINT",EDGE,{"derivedFrom":sQuery(id+"F0.wireOp",EDGE,"E1")}),-1.0]])]});
            var Q7;
            {var subQ1=sQuery(id+"F0.wireOp",EDGE,"E270");Q7=makeQuery(id+"F0.imprint","IMPRINT",FACE,{"disambiguationData":[TD([[makeQuery(id+"F0.imprint","IMPRINT",EDGE,{"derivedFrom":subQ1}),-1.0]])]});}
            var Q8;
            Q8=makeQuery(id+"F0.imprint","IMPRINT",FACE,{"disambiguationData":[TD([[makeQuery(id+"F0.imprint","IMPRINT",EDGE,{"derivedFrom":sQuery(id+"F0.wireOp",EDGE,"E184.MirrorCS")}),-1.0]])]});
            var Q9;
            Q9=makeQuery(id+"F0.imprint","IMPRINT",FACE,{"disambiguationData":[TD([[makeQuery(id+"F0.imprint","IMPRINT",EDGE,{"derivedFrom":sQuery(id+"F0.wireOp",EDGE,"E206.MirrorCS")}),-1.0]])]});
            var Q10;
            {var subQ12=sQuery(id+"F0.wireOp",EDGE,"E99.MirrorCS");Q10=makeQuery(id+"F0.imprint","IMPRINT",FACE,{"disambiguationData":[TD([[makeQuery(id+"F0.imprint","IMPRINT",EDGE,{"derivedFrom":subQ12}),-1.0]])]});}
            var Q11;
            {var subQ22=sQuery(id+"F0.wireOp",EDGE,"E106.MirrorCS");Q11=makeQuery(id+"F0.imprint","IMPRINT",FACE,{"disambiguationData":[TD([[makeQuery(id+"F0.imprint","IMPRINT",EDGE,{"derivedFrom":subQ22}),1.0]])]});}
            var Q12;
            {var subQ20=sQuery(id+"F0.wireOp",EDGE,"E5");Q12=makeQuery(id+"F0.imprint","IMPRINT",FACE,{"disambiguationData":[TD([[makeQuery(id+"F0.imprint","IMPRINT",EDGE,{"derivedFrom":subQ20}),-1.0]])]});}
            var Q13;
            {var subQ12=sQuery(id+"F0.wireOp",EDGE,"E0.bottom");Q13=makeQuery(id+"F0.imprint","IMPRINT",FACE,{"disambiguationData":[TD([[makeQuery(id+"F0.imprint","IMPRINT",EDGE,{"derivedFrom":subQ12}),1.0]])]});}
            var Q14;
            {var subQ3=sQuery(id+"F0.wireOp",EDGE,"E88");Q14=makeQuery(id+"F0.imprint","IMPRINT",FACE,{"disambiguationData":[TD([[makeQuery(id+"F0.imprint","IMPRINT",EDGE,{"derivedFrom":subQ3}),-1.0]])]});}
            var Q15;
            {var subQ1=sQuery(id+"F0.wireOp",EDGE,"E91");Q15=makeQuery(id+"F0.imprint","IMPRINT",FACE,{"disambiguationData":[TD([[makeQuery(id+"F0.imprint","IMPRINT",EDGE,{"derivedFrom":subQ1}),1.0]])]});}
            extrude(context, id + "F1", {"entities" : qUnion([Q0, Q1, Q2, Q3, Q4, Q5, Q6, Q7, Q8, Q9, Q10, Q11, Q12, Q13, Q14, Q15]), "depth" : 2 * mm});
        }
    });
